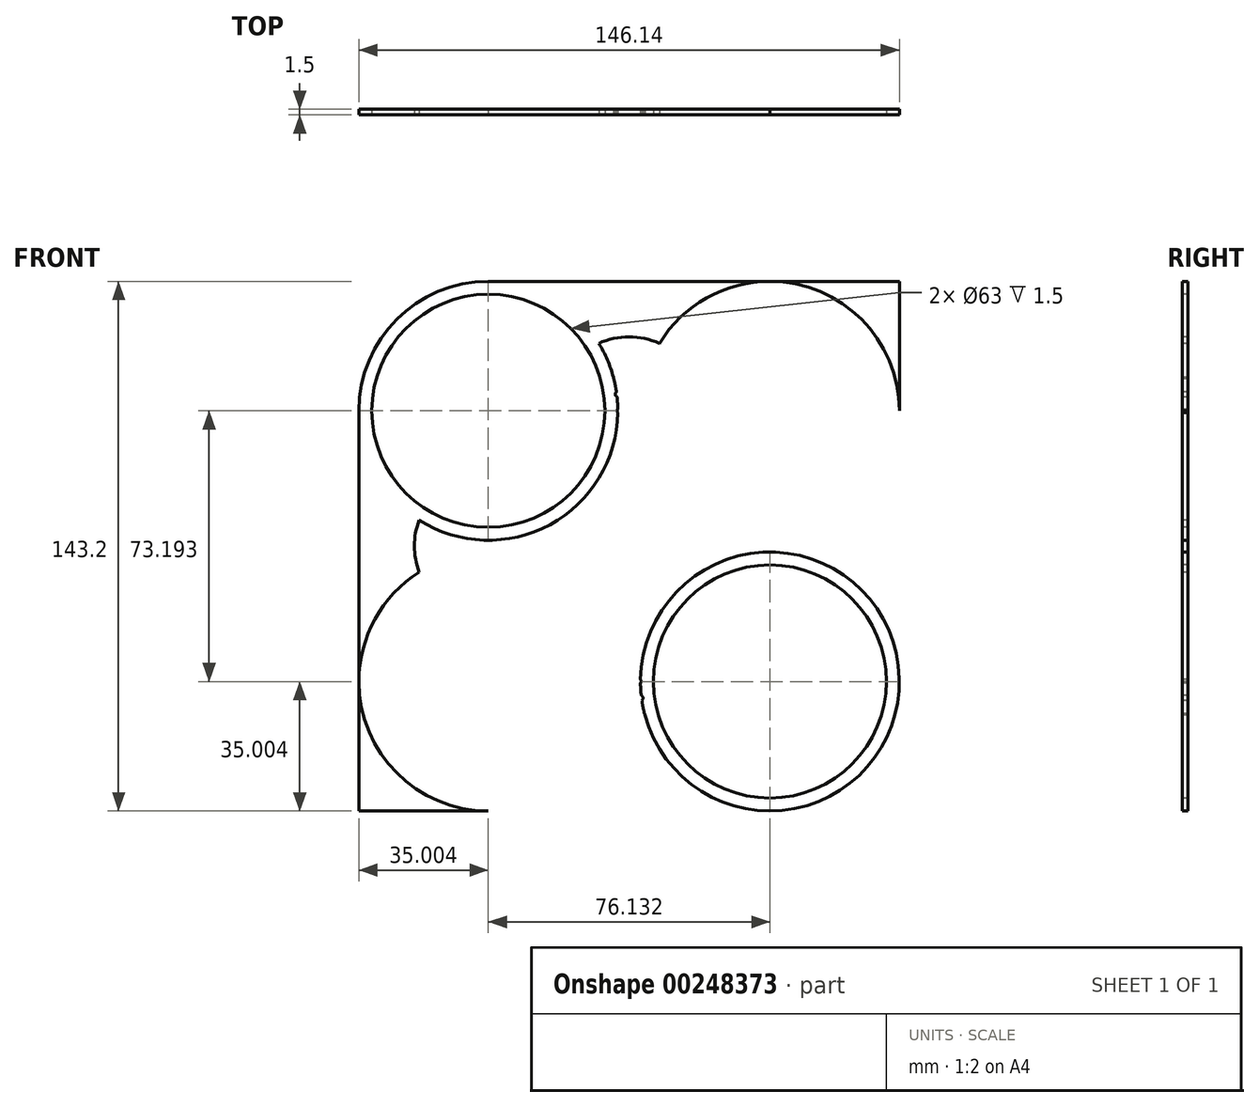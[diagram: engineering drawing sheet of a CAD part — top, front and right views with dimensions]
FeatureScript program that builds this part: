
annotation { "Feature Type Name" : "Feature", "Feature Type Description" : "" }
export const myFeature = defineFeature(function(context is Context, id is Id, definition is map)
    precondition{}
    {
        {
            var Q0;
            Q0=qCreatedBy(makeId("Front.planeOp"),FACE);
            var sketch = newSketch(context, id + "F0", { "sketchPlane" : qUnion([Q0])});
            skLineSegment(sketch, "E0.bottom", {"start": v(-73.07, 71.6) * mm, "end": v(73.07, 71.6) * mm});
            skLineSegment(sketch, "E0.top", {"start": v(-73.07, -71.6) * mm, "end": v(73.07, -71.6) * mm});
            skLineSegment(sketch, "E0.left", {"start": v(-73.07, 71.6) * mm, "end": v(-73.07, -71.6) * mm});
            skLineSegment(sketch, "E0.right", {"start": v(73.07, 71.6) * mm, "end": v(73.07, -71.6) * mm});
            skPoint(sketch, "E0.middle", {"position": v(0, 0) * mm});
            skSolve(sketch);
        }
        {
            var Q0;
            Q0 = qSketchRegion(id + "F0", true);
            extrude(context, id + "F1", {"entities" : qUnion([Q0]), "depth" : 1.5 * mm});
        }
        {
            var Q0;
            Q0=makeQuery(id+"F1.opExtrude","CAP_FACE",FACE,{"disambiguationData":[OSD([sQuery(id+"F0.wireOp",EDGE,"E0.bottom"),sQuery(id+"F0.wireOp",EDGE,"E0.top"),sQuery(id+"F0.wireOp",EDGE,"E0.left"),sQuery(id+"F0.wireOp",EDGE,"E0.right")])],"isStart":false});
            var sketch = newSketch(context, id + "F2", { "sketchPlane" : qUnion([Q0])});
            skCircle(sketch, "E1", {"center": v(-38.07, 36.6) * mm, "radius": 35 * mm});
            skCircle(sketch, "E2.MirrorC", {"center": v(38.07, 36.6) * mm, "radius": 35 * mm});
            skCircle(sketch, "E3.MirrorC", {"center": v(38.07, -36.6) * mm, "radius": 35 * mm});
            skCircle(sketch, "E4.MirrorC", {"center": v(-38.07, -36.6) * mm, "radius": 35 * mm});
            skArc(sketch, "E5", {"start": v(-8.2, 54.84) * mm, "mid": v(0, 56.6) * mm, "end": v(8.2, 54.84) * mm});
            skArc(sketch, "E6", {"start": v(-56.8, 7.03) * mm, "mid": v(-58.07, 0) * mm, "end": v(-56.8, -7.03) * mm});
            skArc(sketch, "E7.MirrorCS", {"start": v(-8.2, -54.84) * mm, "mid": v(0, -56.6) * mm, "end": v(8.2, -54.84) * mm});
            skArc(sketch, "E8.MirrorCS", {"start": v(-56.8, -7.03) * mm, "mid": v(-58.07, 0) * mm, "end": v(-56.8, 7.03) * mm});
            skArc(sketch, "E9.MirrorCS", {"start": v(56.8, -7.03) * mm, "mid": v(58.07, 0) * mm, "end": v(56.8, 7.03) * mm});
            skSolve(sketch);
        }
        {
            var Q0;
            {var subQ0=sQuery(id+"F2.wireOp",EDGE,"E4.MirrorC");var subQ1=makeQuery(id+"F1.opExtrude","CAP_EDGE",EDGE,{"disambiguationData":[OSD([sQuery(id+"F0.wireOp",EDGE,"E0.top")])],"isStart":false});var subQ2=makeQuery(id+"F2.imprint","INTERSECT",VERTEX,{"derivedFrom":[subQ1,subQ0]});Q0=makeQuery(id+"F2.imprint","IMPRINT",FACE,{"disambiguationData":[TD([[makeQuery(id+"F2.imprint","IMPRINT",EDGE,{"disambiguationData":[TD([[subQ2,-1.0]])],"derivedFrom":subQ0}),1.0]])]});}
            var Q1;
            {var subQ0=sQuery(id+"F2.wireOp",EDGE,"E8.MirrorCS");Q1=makeQuery(id+"F2.imprint","IMPRINT",FACE,{"disambiguationData":[TD([[makeQuery(id+"F2.imprint","IMPRINT",EDGE,{"derivedFrom":subQ0}),1.0]])]});}
            var Q2;
            {var subQ0=sQuery(id+"F2.wireOp",EDGE,"E1");var subQ1=makeQuery(id+"F1.opExtrude","CAP_EDGE",EDGE,{"disambiguationData":[OSD([sQuery(id+"F0.wireOp",EDGE,"E0.bottom")])],"isStart":false});var subQ2=makeQuery(id+"F2.imprint","INTERSECT",VERTEX,{"derivedFrom":[subQ1,subQ0]});Q2=makeQuery(id+"F2.imprint","IMPRINT",FACE,{"disambiguationData":[TD([[makeQuery(id+"F2.imprint","IMPRINT",EDGE,{"disambiguationData":[TD([[subQ2,-1.0]])],"derivedFrom":subQ0}),-1.0]])]});}
            var Q3;
            {var subQ0=sQuery(id+"F2.wireOp",EDGE,"E5");Q3=makeQuery(id+"F2.imprint","IMPRINT",FACE,{"disambiguationData":[TD([[makeQuery(id+"F2.imprint","IMPRINT",EDGE,{"derivedFrom":subQ0}),1.0]])]});}
            var Q4;
            {var subQ0=sQuery(id+"F2.wireOp",EDGE,"E9.MirrorCS");Q4=makeQuery(id+"F2.imprint","IMPRINT",FACE,{"disambiguationData":[TD([[makeQuery(id+"F2.imprint","IMPRINT",EDGE,{"derivedFrom":subQ0}),-1.0]])]});}
            var Q5;
            {var subQ0=sQuery(id+"F2.wireOp",EDGE,"E3.MirrorC");var subQ1=makeQuery(id+"F1.opExtrude","CAP_EDGE",EDGE,{"disambiguationData":[OSD([sQuery(id+"F0.wireOp",EDGE,"E0.top")])],"isStart":false});var subQ2=makeQuery(id+"F2.imprint","INTERSECT",VERTEX,{"derivedFrom":[subQ1,subQ0]});Q5=makeQuery(id+"F2.imprint","IMPRINT",FACE,{"disambiguationData":[TD([[makeQuery(id+"F2.imprint","IMPRINT",EDGE,{"disambiguationData":[TD([[subQ2,-1.0]])],"derivedFrom":subQ0}),-1.0]])]});}
            var Q6;
            {var subQ0=sQuery(id+"F2.wireOp",EDGE,"E7.MirrorCS");Q6=makeQuery(id+"F2.imprint","IMPRINT",FACE,{"disambiguationData":[TD([[makeQuery(id+"F2.imprint","IMPRINT",EDGE,{"derivedFrom":subQ0}),-1.0]])]});}
            var Q7;
            {var subQ0=sQuery(id+"F2.wireOp",EDGE,"E2.MirrorC");var subQ1=makeQuery(id+"F1.opExtrude","CAP_EDGE",EDGE,{"disambiguationData":[OSD([sQuery(id+"F0.wireOp",EDGE,"E0.bottom")])],"isStart":false});var subQ2=makeQuery(id+"F2.imprint","INTERSECT",VERTEX,{"derivedFrom":[subQ1,subQ0]});Q7=makeQuery(id+"F2.imprint","IMPRINT",FACE,{"disambiguationData":[TD([[makeQuery(id+"F2.imprint","IMPRINT",EDGE,{"disambiguationData":[TD([[subQ2,-1.0]])],"derivedFrom":subQ0}),1.0]])]});}
            extrude(context, id + "F3", {"entities" : qUnion([Q0, Q1, Q2, Q3, Q4, Q5, Q6, Q7]), "operationType" : NewBodyOperationType.REMOVE, "oppositeDirection" : true, "depth" : 25 * mm});
        }
        {
            var Q0;
            Q0=makeQuery(id+"F1.opExtrude","CAP_FACE",FACE,{"disambiguationData":[OSD([sQuery(id+"F0.wireOp",EDGE,"E0.bottom"),sQuery(id+"F0.wireOp",EDGE,"E0.top"),sQuery(id+"F0.wireOp",EDGE,"E0.left"),sQuery(id+"F0.wireOp",EDGE,"E0.right")])],"isStart":false});
            var sketch = newSketch(context, id + "F4", { "sketchPlane" : qUnion([Q0])});
            skCircle(sketch, "E10", {"center": v(-38.07, 36.6) * mm, "radius": 31.5 * mm});
            skCircle(sketch, "E11.MirrorC", {"center": v(38.07, 36.6) * mm, "radius": 31.5 * mm});
            skCircle(sketch, "E12.MirrorC", {"center": v(38.07, -36.6) * mm, "radius": 31.5 * mm});
            skCircle(sketch, "E13.MirrorC", {"center": v(-38.07, -36.6) * mm, "radius": 31.5 * mm});
            skSolve(sketch);
        }
        {
            var Q0;
            Q0 = qSketchRegion(id + "F4", true);
            extrude(context, id + "F5", {"entities" : qUnion([Q0]), "operationType" : NewBodyOperationType.REMOVE, "oppositeDirection" : true, "depth" : 25 * mm});
        }
        {
            var Q0;
            {var subQ5=sQuery(id+"F2.wireOp",EDGE,"E5");Q0=makeQuery(id+"F2.imprint","IMPRINT",FACE,{"disambiguationData":[TD([[makeQuery(id+"F2.imprint","IMPRINT",EDGE,{"derivedFrom":subQ5}),-1.0]])]});}
            var sketch = newSketch(context, id + "F6", { "sketchPlane" : qUnion([Q0])});
            skEllipse(sketch, "E14", {"center": v(0, 50.07) * mm, "majorRadius": 4.75 * mm, "minorRadius": 1.5 * mm, "majorAxis": v(-1, 0)});
            skEllipse(sketch, "E15", {"center": v(0, 45.57) * mm, "majorRadius": 4.25 * mm, "minorRadius": 1.5 * mm, "majorAxis": v(-1, 0)});
            skEllipse(sketch, "E16", {"center": v(0, 41.07) * mm, "majorRadius": 3.75 * mm, "minorRadius": 1.5 * mm, "majorAxis": v(-1, 0)});
            skEllipse(sketch, "E17", {"center": v(0, 36.57) * mm, "majorRadius": 3.25 * mm, "minorRadius": 1.5 * mm, "majorAxis": v(-1, 0)});
            skEllipse(sketch, "E18", {"center": v(0, 32.07) * mm, "majorRadius": 3 * mm, "minorRadius": 1.5 * mm, "majorAxis": v(-1, 0)});
            skEllipse(sketch, "E19.MirrorC", {"center": v(0, -36.57) * mm, "majorRadius": 3.25 * mm, "minorRadius": 1.5 * mm, "majorAxis": v(-1, 0)});
            skEllipse(sketch, "E20.MirrorC", {"center": v(0, -50.07) * mm, "majorRadius": 4.75 * mm, "minorRadius": 1.5 * mm, "majorAxis": v(-1, 0)});
            skEllipse(sketch, "E21.MirrorC", {"center": v(0, -32.07) * mm, "majorRadius": 3 * mm, "minorRadius": 1.5 * mm, "majorAxis": v(-1, 0)});
            skEllipse(sketch, "E22.MirrorC", {"center": v(0, -45.57) * mm, "majorRadius": 4.25 * mm, "minorRadius": 1.5 * mm, "majorAxis": v(-1, 0)});
            skEllipse(sketch, "E23.MirrorC", {"center": v(0, -41.07) * mm, "majorRadius": 3.75 * mm, "minorRadius": 1.5 * mm, "majorAxis": v(-1, 0)});
            skSolve(sketch);
        }
        {
            var Q0;
            Q0 = qSketchRegion(id + "F6", true);
            extrude(context, id + "F7", {"entities" : qUnion([Q0]), "operationType" : NewBodyOperationType.REMOVE, "oppositeDirection" : true, "depth" : 25 * mm});
        }
    });
